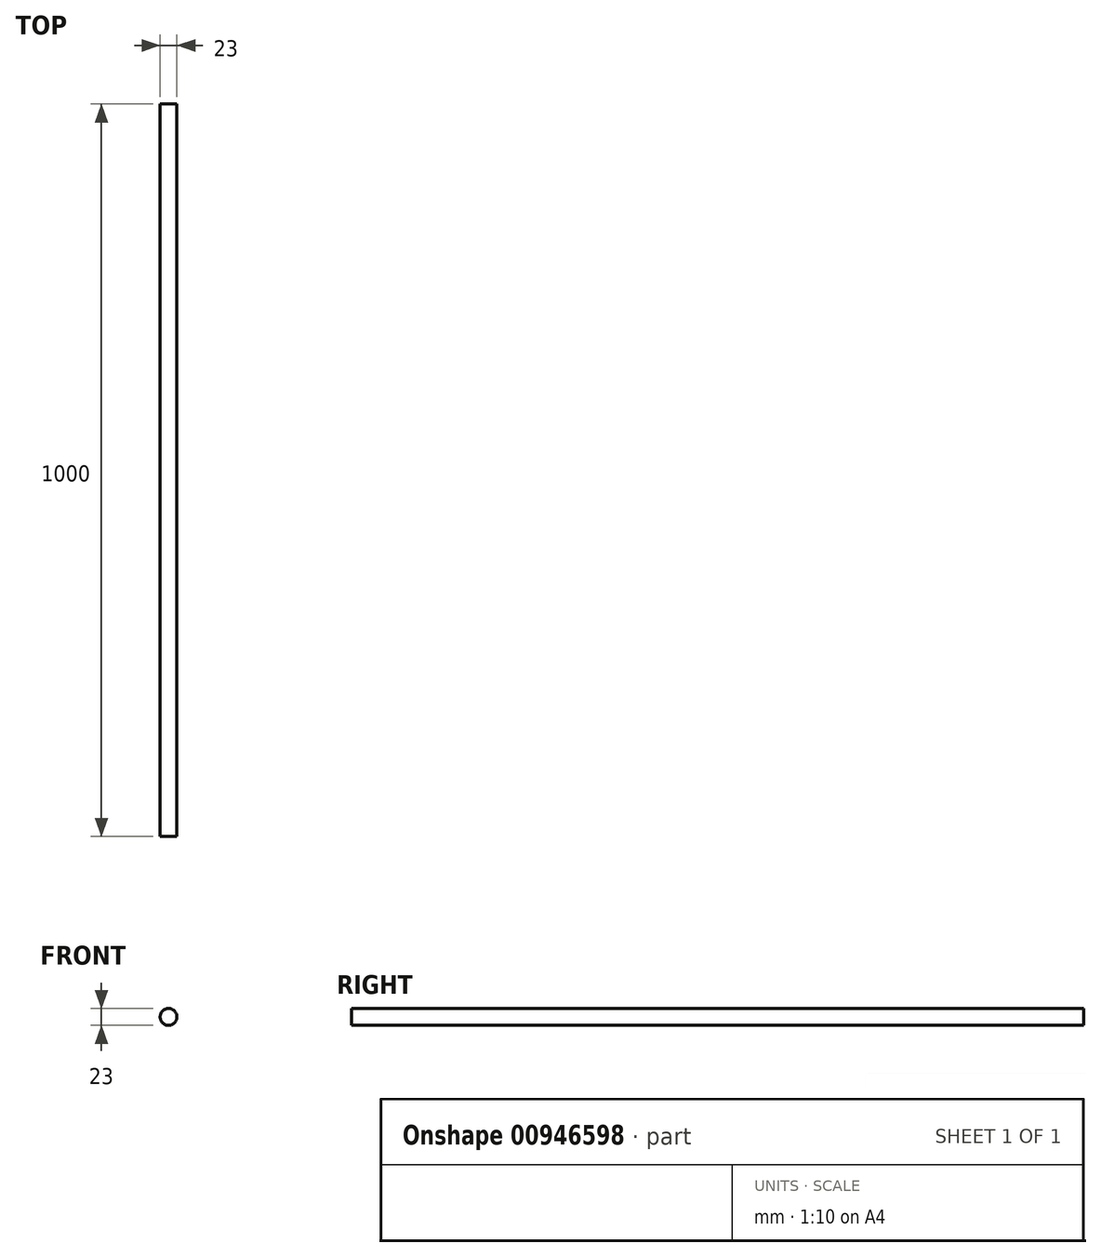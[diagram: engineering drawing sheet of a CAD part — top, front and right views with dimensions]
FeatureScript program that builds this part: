
annotation { "Feature Type Name" : "Feature", "Feature Type Description" : "" }
export const myFeature = defineFeature(function(context is Context, id is Id, definition is map)
    precondition{}
    {
        {
            var Q0;
            Q0=qCreatedBy(makeId("Front.planeOp"),FACE);
            var sketch = newSketch(context, id + "F0", { "sketchPlane" : qUnion([Q0])});
            skCircle(sketch, "E0", {"center": v(0, 0) * mm, "radius": 11.5 * mm});
            skSolve(sketch);
        }
        {
            var Q0;
            Q0 = qSketchRegion(id + "F0", true);
            extrude(context, id + "F1", {"entities" : qUnion([Q0]), "depth" : 1000 * mm, "offsetDistance" : 25 * mm});
        }
    });
